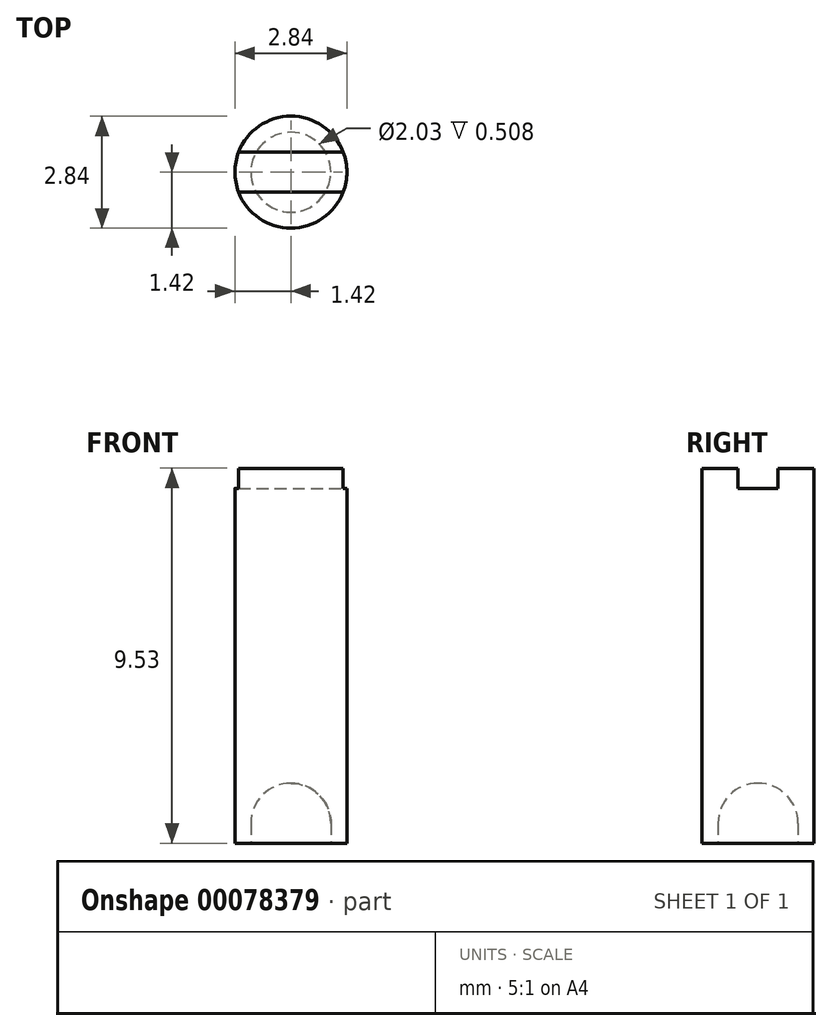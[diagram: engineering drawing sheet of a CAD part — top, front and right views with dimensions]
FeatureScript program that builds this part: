
annotation { "Feature Type Name" : "Feature", "Feature Type Description" : "" }
export const myFeature = defineFeature(function(context is Context, id is Id, definition is map)
    precondition{}
    {
        {
            var Q0;
            Q0=qCreatedBy(makeId("Top.planeOp"),FACE);
            var sketch = newSketch(context, id + "F0", { "sketchPlane" : qUnion([Q0])});
            skCircle(sketch, "E0", {"center": v(0, 0) * mm, "radius": 1.42 * mm});
            skSolve(sketch);
        }
        {
            var Q0;
            Q0 = qSketchRegion(id + "F0", true);
            extrude(context, id + "F1", {"entities" : qUnion([Q0]), "depth" : 9.52 * mm});
        }
        {
            var Q0;
            Q0=qCreatedBy(makeId("Front.planeOp"),FACE);
            var sketch = newSketch(context, id + "F2", { "sketchPlane" : qUnion([Q0])});
            skLineSegment(sketch, "E1", {"start": v(0, 0) * mm, "end": v(0, 1.52) * mm});
            skArc(sketch, "E2", {"start": v(1.02, 0.5) * mm, "mid": v(0.72, 1.23) * mm, "end": v(0, 1.52) * mm});
            skLineSegment(sketch, "E3", {"start": v(1.02, 0.5) * mm, "end": v(1.02, 0) * mm});
            skLineSegment(sketch, "E4", {"start": v(1.02, 0) * mm, "end": v(0, 0) * mm});
            skSolve(sketch);
        }
        {
            var Q0;
            Q0 = qSketchRegion(id + "F2", true);
            var Q1;
            Q1=makeQuery(id+"F1.opExtrude","SWEPT_FACE",FACE,{"disambiguationData":[OSD([sQuery(id+"F0.wireOp",EDGE,"E0")])]});
            revolve(context, id + "F3", {"operationType" : NewBodyOperationType.REMOVE, "entities" : qUnion([Q0]), "axis" : qUnion([Q1]), "revolveType" : RevolveType.FULL, "oppositeDirection" : true});
        }
        {
            var Q0;
            Q0=makeQuery(id+"F1.opExtrude","CAP_FACE",FACE,{"disambiguationData":[OSD([sQuery(id+"F0.wireOp",EDGE,"E0")])],"isStart":false});
            var sketch = newSketch(context, id + "F4", { "sketchPlane" : qUnion([Q0])});
            skLineSegment(sketch, "E5", {"start": v(0, 0.5) * mm, "end": v(1.96, 0.5) * mm});
            skLineSegment(sketch, "E6.MirrorCS", {"start": v(0, 0.5) * mm, "end": v(-1.96, 0.5) * mm});
            skLineSegment(sketch, "E7.MirrorCS", {"start": v(0, -0.5) * mm, "end": v(1.96, -0.5) * mm});
            skLineSegment(sketch, "E8.MirrorCS", {"start": v(0, -0.5) * mm, "end": v(-1.96, -0.5) * mm});
            skLineSegment(sketch, "E9", {"start": v(-1.96, 0.5) * mm, "end": v(-1.96, -0.5) * mm});
            skLineSegment(sketch, "E10", {"start": v(1.96, 0.5) * mm, "end": v(1.96, -0.5) * mm});
            skSolve(sketch);
        }
        {
            var Q0;
            Q0 = qSketchRegion(id + "F4", true);
            extrude(context, id + "F5", {"entities" : qUnion([Q0]), "operationType" : NewBodyOperationType.REMOVE, "oppositeDirection" : true, "depth" : 0.5 * mm});
        }
    });
